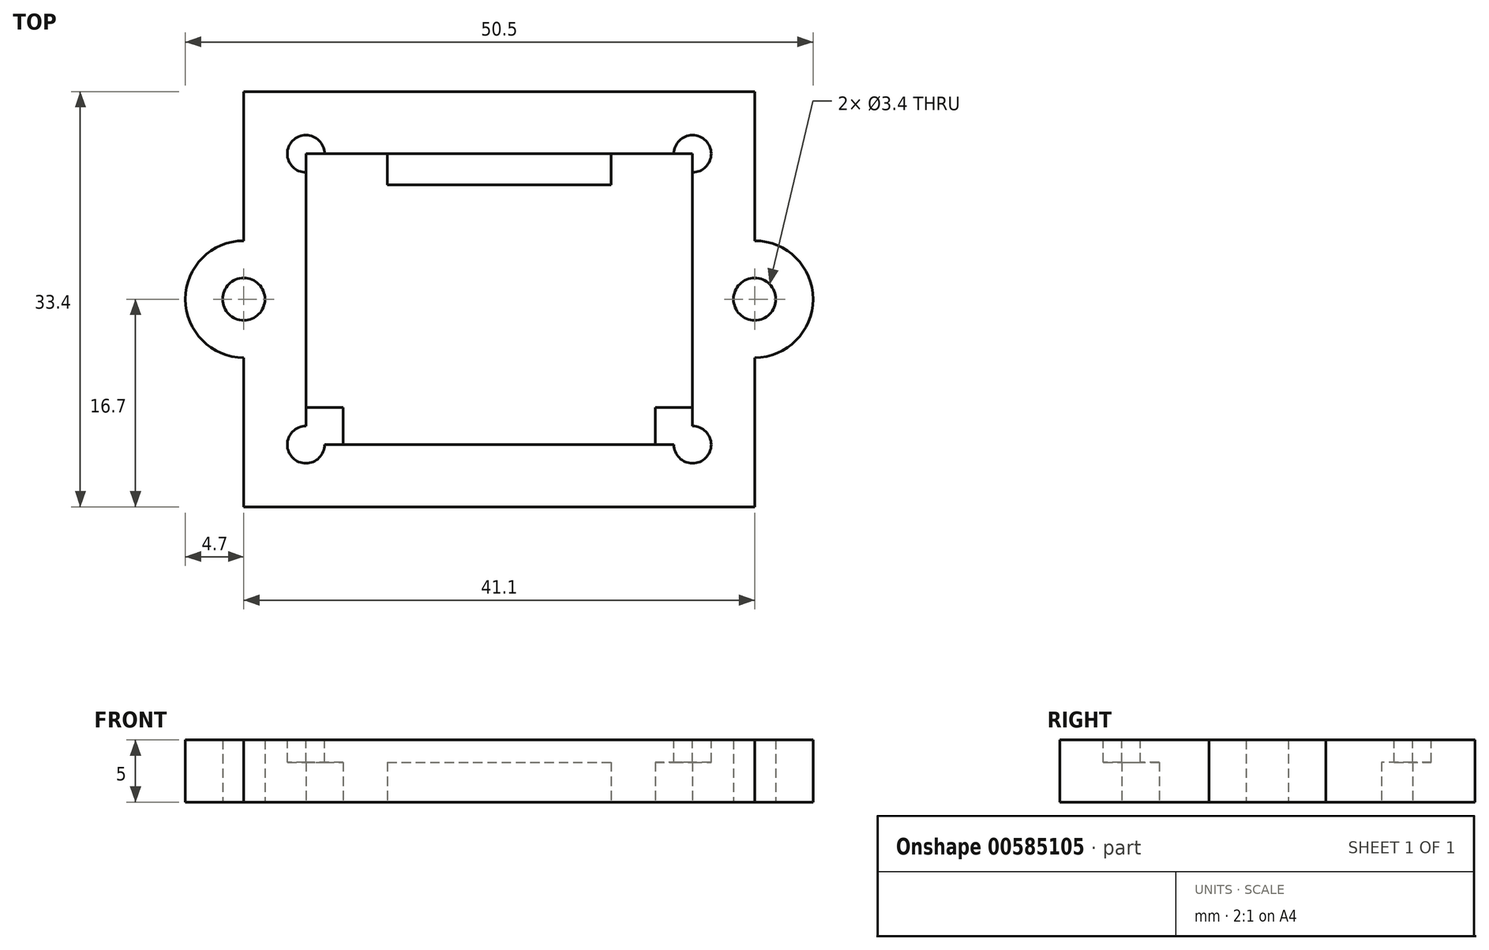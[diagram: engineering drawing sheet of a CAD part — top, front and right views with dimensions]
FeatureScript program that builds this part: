
annotation { "Feature Type Name" : "Feature", "Feature Type Description" : "" }
export const myFeature = defineFeature(function(context is Context, id is Id, definition is map)
    precondition{}
    {
        {
            var Q0;
            Q0=qCreatedBy(makeId("Top.planeOp"),FACE);
            var sketch = newSketch(context, id + "F0", { "sketchPlane" : qUnion([Q0])});
            skLineSegment(sketch, "E0.top", {"start": v(-9, 9.2) * mm, "end": v(9, 9.2) * mm});
            skPoint(sketch, "E0.middle", {"position": v(0, 0) * mm});
            skLineSegment(sketch, "E1.bottom", {"start": v(-20.55, -16.7) * mm, "end": v(20.55, -16.7) * mm});
            skLineSegment(sketch, "E1.top", {"start": v(-20.55, 16.7) * mm, "end": v(20.55, 16.7) * mm});
            skLineSegment(sketch, "E1.left", {"start": v(-20.55, -16.7) * mm, "end": v(-20.55, -4.7) * mm});
            skLineSegment(sketch, "E1.right", {"start": v(20.55, -16.7) * mm, "end": v(20.55, -4.7) * mm});
            skLineSegment(sketch, "E2", {"start": v(-12.55, -8.7) * mm, "end": v(-12.55, -11.7) * mm});
            skLineSegment(sketch, "E3", {"start": v(-12.55, -11.7) * mm, "end": v(12.55, -11.7) * mm});
            skLineSegment(sketch, "E4", {"start": v(12.55, -11.7) * mm, "end": v(12.55, -8.7) * mm});
            skLineSegment(sketch, "E5", {"start": v(-12.55, -8.7) * mm, "end": v(-15.55, -8.7) * mm});
            skLineSegment(sketch, "E6", {"start": v(-15.55, -8.7) * mm, "end": v(-15.55, 11.7) * mm});
            skLineSegment(sketch, "E7", {"start": v(-15.55, 11.7) * mm, "end": v(-9, 11.7) * mm});
            skLineSegment(sketch, "E8", {"start": v(9, 11.7) * mm, "end": v(15.55, 11.7) * mm});
            skLineSegment(sketch, "E9", {"start": v(15.55, 11.7) * mm, "end": v(15.55, -8.7) * mm});
            skLineSegment(sketch, "E10", {"start": v(15.55, -8.7) * mm, "end": v(12.55, -8.7) * mm});
            skLineSegment(sketch, "E11", {"start": v(9, 11.7) * mm, "end": v(9, 9.2) * mm});
            skLineSegment(sketch, "E12", {"start": v(-9, 11.7) * mm, "end": v(-9, 9.2) * mm});
            skPoint(sketch, "E13.orphan", {"position": v(-14, 9.2) * mm});
            skPoint(sketch, "E14.orphan", {"position": v(14, 9.2) * mm});
            skLineSegment(sketch, "E15", {"start": v(0, 0) * mm, "end": v(-15.55, 0) * mm, "construction": true});
            skLineSegment(sketch, "E16", {"start": v(0, 0) * mm, "end": v(15.55, 0) * mm, "construction": true});
            skLineSegment(sketch, "E17", {"start": v(0, -11.7) * mm, "end": v(0, 0) * mm, "construction": true});
            skLineSegment(sketch, "E18", {"start": v(11.62, 11.7) * mm, "end": v(11.62, 0) * mm, "construction": true});
            skArc(sketch, "E19", {"start": v(-20.55, 4.7) * mm, "mid": v(-25.25, 0) * mm, "end": v(-20.55, -4.7) * mm});
            skLineSegment(sketch, "E20", {"start": v(-20.55, 4.7) * mm, "end": v(-20.55, 4.7) * mm});
            skLineSegment(sketch, "E21", {"start": v(-20.55, -4.7) * mm, "end": v(-20.55, -4.7) * mm});
            skLineSegment(sketch, "E22.trimOffspring", {"start": v(-20.55, 4.7) * mm, "end": v(-20.55, 16.7) * mm});
            skCircle(sketch, "E23", {"center": v(-20.55, 0) * mm, "radius": 1.7 * mm});
            skCircle(sketch, "E24.MirrorC", {"center": v(20.55, 0) * mm, "radius": 1.7 * mm});
            skArc(sketch, "E25.MirrorCS", {"start": v(20.55, 4.7) * mm, "mid": v(25.25, 0) * mm, "end": v(20.55, -4.7) * mm});
            skLineSegment(sketch, "E26.MirrorCS", {"start": v(20.55, 4.7) * mm, "end": v(20.55, 4.7) * mm});
            skLineSegment(sketch, "E27.MirrorCS", {"start": v(20.55, -4.7) * mm, "end": v(20.55, -4.7) * mm});
            skLineSegment(sketch, "E28.trimOffspring", {"start": v(20.55, 4.7) * mm, "end": v(20.55, 16.7) * mm});
            skSolve(sketch);
        }
        {
            var Q0;
            Q0 = qSketchRegion(id + "F0", true);
            extrude(context, id + "F1", {"entities" : qUnion([Q0]), "depth" : 5 * mm, "offsetDistance" : 25 * mm});
        }
        {
            var Q0;
            Q0=makeQuery(id+"F1.opExtrude","CAP_FACE",FACE,{"disambiguationData":[OSD([sQuery(id+"F0.wireOp",EDGE,"E0.bottom"),sQuery(id+"F0.wireOp",EDGE,"E0.top"),sQuery(id+"F0.wireOp",EDGE,"E0.left"),sQuery(id+"F0.wireOp",EDGE,"E0.right"),sQuery(id+"F0.wireOp",EDGE,"E1.bottom"),sQuery(id+"F0.wireOp",EDGE,"E1.top"),sQuery(id+"F0.wireOp",EDGE,"E1.left"),sQuery(id+"F0.wireOp",EDGE,"E1.right"),sQuery(id+"F0.wireOp",EDGE,"E2"),sQuery(id+"F0.wireOp",EDGE,"E3"),sQuery(id+"F0.wireOp",EDGE,"E4"),sQuery(id+"F0.wireOp",EDGE,"395f1d7f-0e0a-45c6-8681-77e3a7d31e22.trimOffspring"),sQuery(id+"F0.wireOp",EDGE,"E5"),sQuery(id+"F0.wireOp",EDGE,"E6"),sQuery(id+"F0.wireOp",EDGE,"E7"),sQuery(id+"F0.wireOp",EDGE,"E8"),sQuery(id+"F0.wireOp",EDGE,"E9"),sQuery(id+"F0.wireOp",EDGE,"E10"),sQuery(id+"F0.wireOp",EDGE,"E11"),sQuery(id+"F0.wireOp",EDGE,"E12")])],"isStart":false});
            var sketch = newSketch(context, id + "F2", { "sketchPlane" : qUnion([Q0])});
            skLineSegment(sketch, "E29.bottom", {"start": v(-14.05, 11.7) * mm, "end": v(14.05, 11.7) * mm});
            skLineSegment(sketch, "E29.top", {"start": v(-14.05, -11.7) * mm, "end": v(14.05, -11.7) * mm});
            skLineSegment(sketch, "E29.left", {"start": v(-15.55, 10.2) * mm, "end": v(-15.55, -10.2) * mm});
            skLineSegment(sketch, "E29.right", {"start": v(15.55, 10.2) * mm, "end": v(15.55, -10.2) * mm});
            skArc(sketch, "E30", {"start": v(-15.55, -10.2) * mm, "mid": v(-16.61, -12.76) * mm, "end": v(-14.05, -11.7) * mm});
            skArc(sketch, "E31", {"start": v(14.05, -11.7) * mm, "mid": v(16.61, -12.76) * mm, "end": v(15.55, -10.2) * mm});
            skArc(sketch, "E32", {"start": v(15.55, 10.2) * mm, "mid": v(16.61, 12.76) * mm, "end": v(14.05, 11.7) * mm});
            skArc(sketch, "E33", {"start": v(-14.05, 11.7) * mm, "mid": v(-16.61, 12.76) * mm, "end": v(-15.55, 10.2) * mm});
            skSolve(sketch);
        }
        {
            var Q0;
            Q0 = qSketchRegion(id + "F2", true);
            extrude(context, id + "F3", {"entities" : qUnion([Q0]), "operationType" : NewBodyOperationType.REMOVE, "oppositeDirection" : true, "depth" : 1.8 * mm, "offsetDistance" : 25 * mm});
        }
    });
